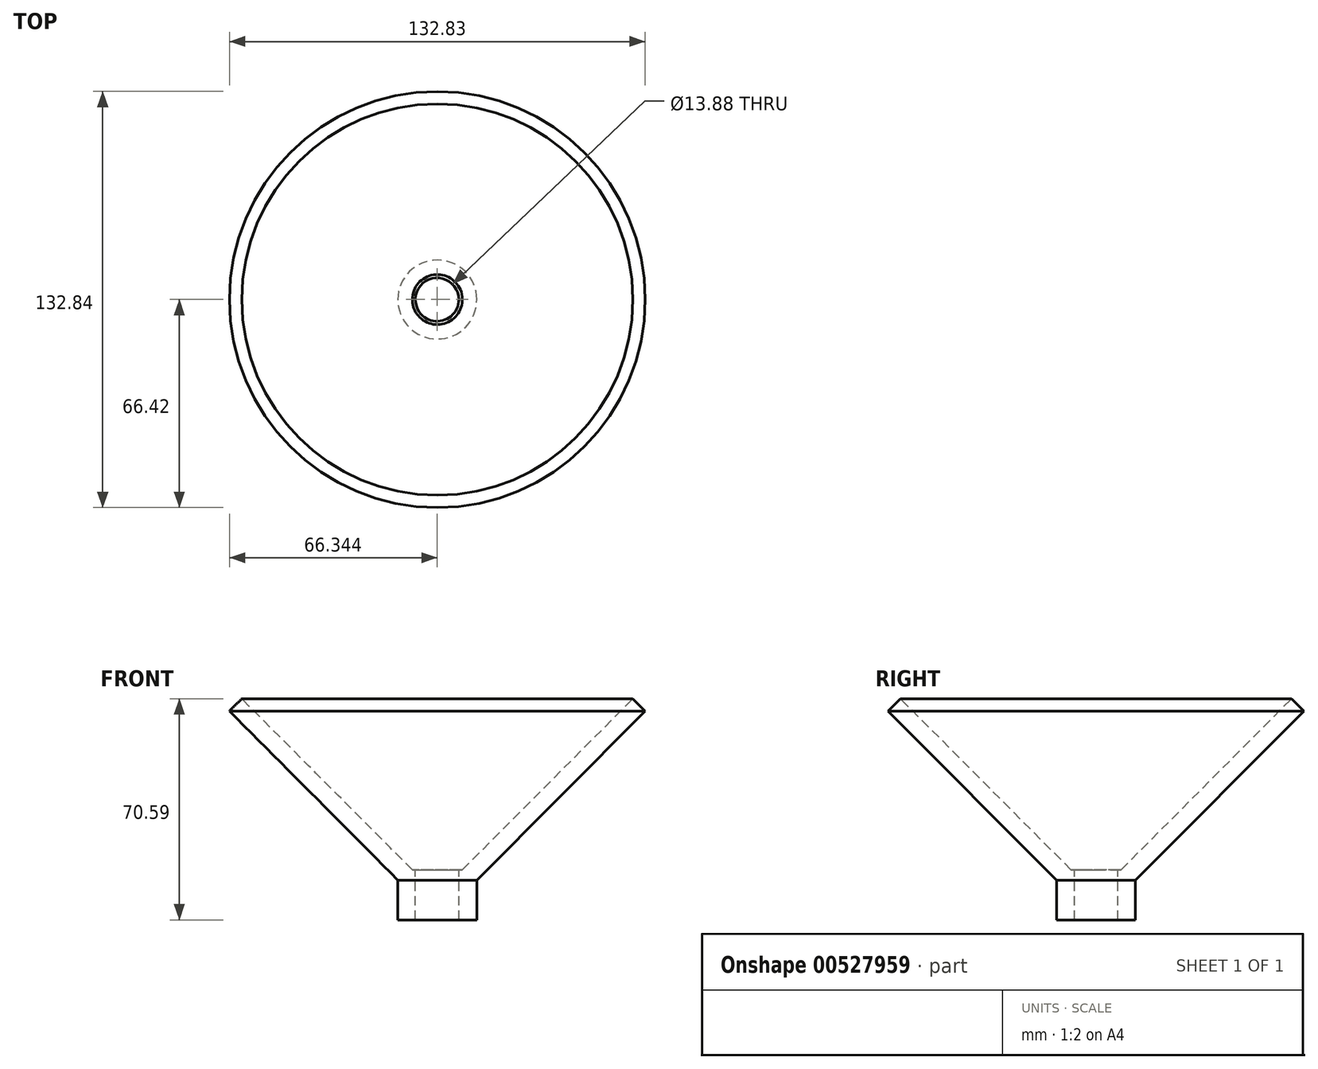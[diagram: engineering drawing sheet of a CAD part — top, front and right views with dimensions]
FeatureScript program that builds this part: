
annotation { "Feature Type Name" : "Feature", "Feature Type Description" : "" }
export const myFeature = defineFeature(function(context is Context, id is Id, definition is map)
    precondition{}
    {
        {
            var Q0;
            Q0=qCreatedBy(makeId("Front.planeOp"),FACE);
            var sketch = newSketch(context, id + "F0", { "sketchPlane" : qUnion([Q0])});
            skLineSegment(sketch, "E0", {"start": v(0, 0) * mm, "end": v(53.81, 53.95) * mm});
            skLineSegment(sketch, "E1", {"start": v(53.81, 53.95) * mm, "end": v(49.87, 57.89) * mm});
            skLineSegment(sketch, "E2", {"start": v(49.87, 57.89) * mm, "end": v(-4.61, 3.27) * mm});
            skLineSegment(sketch, "E3", {"start": v(0, 0) * mm, "end": v(0, -12.7) * mm});
            skLineSegment(sketch, "E4", {"start": v(0, -12.7) * mm, "end": v(-12.6, -12.7) * mm});
            skLineSegment(sketch, "E5", {"start": v(-12.6, -12.7) * mm, "end": v(-12.6, 2.86) * mm});
            skLineSegment(sketch, "E6", {"start": v(-12.6, 2.86) * mm, "end": v(-4.61, 3.27) * mm});
            skSolve(sketch);
        }
        {
            var Q0;
            Q0 = qSketchRegion(id + "F0", true);
            var Q1;
            Q1=sQuery(id+"F0.wireOp",EDGE,"E5");
            revolve(context, id + "F1", {"entities" : qUnion([Q0]), "axis" : qUnion([Q1]), "revolveType" : RevolveType.FULL});
        }
        {
            var Q0;
            Q0=qCreatedBy(makeId("Top.planeOp"),FACE);
            var sketch = newSketch(context, id + "F2", { "sketchPlane" : qUnion([Q0])});
            skCircle(sketch, "E7", {"center": v(-12.68, 0) * mm, "radius": 6.94 * mm});
            skSolve(sketch);
        }
        {
            var Q0;
            Q0 = qSketchRegion(id + "F2", true);
            extrude(context, id + "F3", {"entities" : qUnion([Q0]), "operationType" : NewBodyOperationType.REMOVE, "oppositeDirection" : true, "depth" : 279.4 * mm, "offsetDistance" : 25.4 * mm});
        }
        {
            var Q0;
            Q0 = qSketchRegion(id + "F2", true);
            extrude(context, id + "F4", {"entities" : qUnion([Q0]), "operationType" : NewBodyOperationType.REMOVE, "oppositeDirection" : true, "depth" : -25.4 * mm, "offsetDistance" : 25.4 * mm});
        }
    });
